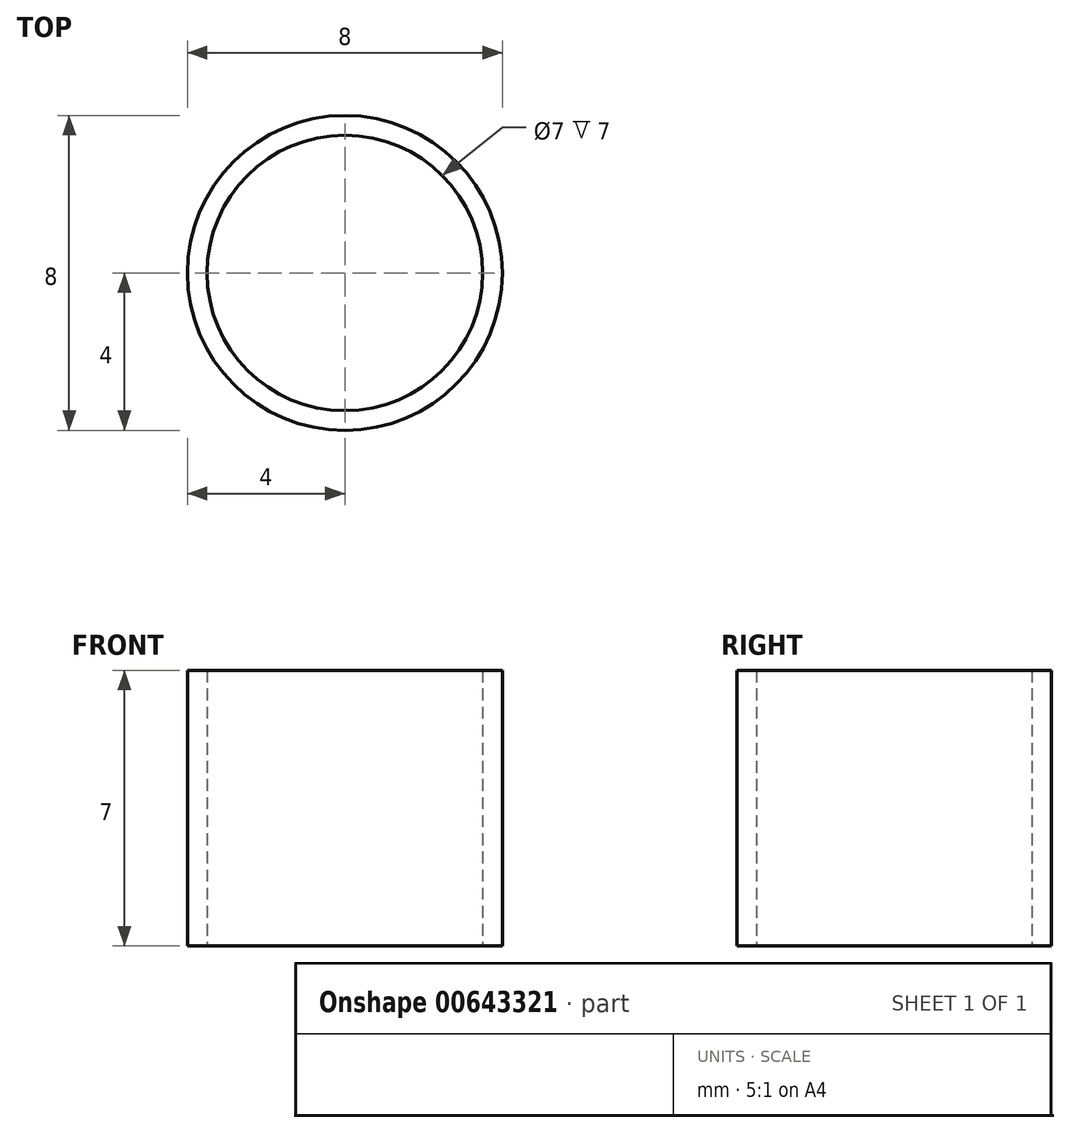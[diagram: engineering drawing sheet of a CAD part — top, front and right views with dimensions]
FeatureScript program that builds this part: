
annotation { "Feature Type Name" : "Feature", "Feature Type Description" : "" }
export const myFeature = defineFeature(function(context is Context, id is Id, definition is map)
    precondition{}
    {
        {
            var Q0;
            Q0=qCreatedBy(makeId("Top.planeOp"),FACE);
            var sketch = newSketch(context, id + "F0", { "sketchPlane" : qUnion([Q0])});
            skCircle(sketch, "E0", {"center": v(0, 0) * mm, "radius": 4 * mm});
            skCircle(sketch, "E1", {"center": v(0, 0) * mm, "radius": 3.5 * mm});
            skSolve(sketch);
        }
        {
            var Q0;
            Q0=makeQuery(id+"F0.imprint","IMPRINT",FACE,{"disambiguationData":[TD([[makeQuery(id+"F0.imprint","IMPRINT",EDGE,{"derivedFrom":sQuery(id+"F0.wireOp",EDGE,"E0")}),1.0]])]});
            extrude(context, id + "F1", {"entities" : qUnion([Q0]), "depth" : 7 * mm, "offsetDistance" : 25.4 * mm});
        }
    });
